# Revit family: LHBV48
name_source: partatom
category: Lighting Fixtures
units: mm (PartAtom-declared; Revit-internal decimal feet)

## family parameters
Always vertical = Yes
Cut with Voids When Loaded = No
Host = Ceiling
Light Source = Yes
OmniClass Number = 23.80.70.11
OmniClass Title = Luminaries for Internal Lighting
Part Type = Normal
Room Calculation Point = No
Round Connector Dimension = Use Diameter
Shared = No

## types (5) — shared parameters
Assembly Code = D5020200
Color Filter = 16777215
Description = LED High Bay Vapour
Dimming Lamp Color Temperature Shift = <None>
Emit from Line Length = 4' - 3 31/32"
Housing Finish = Metal - Viscor - White
Lamp = LED
Length = 4' - 3 31/32"
Lens Finsih = Acrylic - Viscor - High Impact Textured
Manufacturer = VISIONEERING by VISCOR
Model = LHBV
Tilt Angle = 90.00°
URL = https://www.viscor.com
Voltage = 120 V
Width = 1' - 2 9/16"

## per-type parameters (varying)
| type | Apparent Load | Lamp Wattage | Photometric Web File |
| LHBV48-LED840K120LUNV | 79 VA | 79 VA | LHBV48-LED840K120LUNV-P05.IES |
| LHBV48-LED840K150LUNV | 100 VA | 100 VA | LHBV48-LED840K150LUNV-P05.IES |
| LHBV48-LED840K180LUNV | 121 VA | 121 VA | LHBV48-LED840K180LUNV-P05.IES |
| LHBV48-LED840K240LUNV | 158 VA | 158 VA | LHBV48-LED840K240LUNV-P05.IES |
| LHBV48-LED840K300LUNV | 201 VA | 201 VA | LHBV48-LED840K300LUNV-P05.IES |

## geometry (parser evidence)
native form markers: Sweep x3
no freeform markers — native parametric forms only
